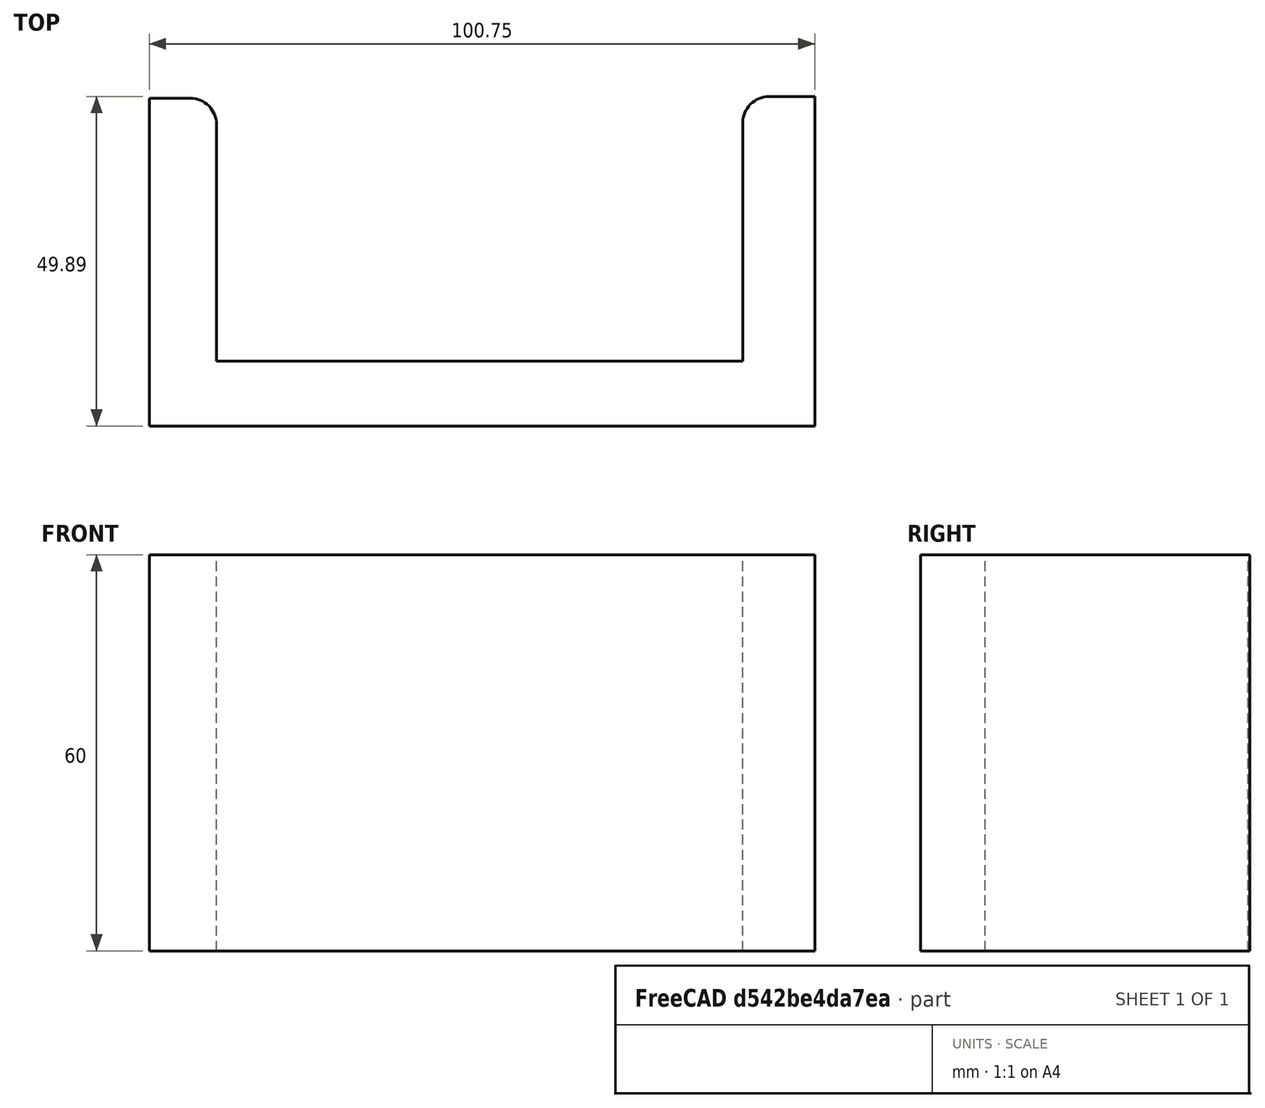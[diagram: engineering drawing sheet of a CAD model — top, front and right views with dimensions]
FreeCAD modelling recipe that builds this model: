
FCSTD DOCUMENT  (FreeCAD 0.21R33668 +26 (Git))
Label: u
License: All rights reserved
LicenseURL: http://en.wikipedia.org/wiki/All_rights_reserved
objects: Part::Extrusion×2, Sketcher::SketchObject×1, Part::Chamfer×1, Part::Fillet×1
note: 5 computed .brp shape members not serialized (recipe doc carries the construction recipe); baked Part::Feature solids carry a one-line shape summary decoded from their .brp

FEATURE [Sketcher::SketchObject] Sketch
  FullyConstrained = false
  sketch-geometry (8):
    g0: LineSegment StartX=-49.9191 StartY=49.6407 StartZ=0 EndX=-49.9191 EndY=0 EndZ=0
    g1: LineSegment StartX=50.8303 StartY=0 StartZ=0 EndX=50.8303 EndY=49.8944 EndZ=0
    g2: LineSegment StartX=39.9179 StartY=49.8944 StartZ=0 EndX=50.8303 EndY=49.8944 EndZ=0
    g3: LineSegment StartX=39.9179 StartY=9.79766 StartZ=0 EndX=39.9179 EndY=49.8944 EndZ=0
    g4: LineSegment StartX=39.9179 StartY=9.79766 StartZ=0 EndX=-39.768 EndY=9.79766 EndZ=0
    g5: LineSegment StartX=-49.9191 StartY=49.6407 StartZ=0 EndX=-39.768 EndY=49.6407 EndZ=0
    g6: LineSegment StartX=-39.768 StartY=49.6407 StartZ=0 EndX=-39.768 EndY=9.79766 EndZ=0
    g7: LineSegment StartX=-49.9191 StartY=0 StartZ=0 EndX=50.8303 EndY=0 EndZ=0
  constraints (17):
    c: PointOnObject(g0,g-1)
    c: Vertical(g0)
    c: PointOnObject(g1,g-1)
    c: Vertical(g1)
    c: Coincident(g2,g1)
    c: Horizontal(g2)
    c: Coincident(g3,g2)
    c: Vertical(g3)
    c: Coincident(g4,g3)
    c: Horizontal(g4)
    c: Coincident(g5,g0)
    c: Horizontal(g5)
    c: Coincident(g6,g5)
    c: Coincident(g6,g4)
    c: Vertical(g6)
    c: Coincident(g7,g0)
    c: Coincident(g7,g1)
FEATURE [Part::Extrusion] Extrude
  Base = -> Sketch
  Dir = (0,0,1)
  DirMode = 2
  FaceMakerClass = Part::FaceMakerBullseye
  LengthFwd = 60
  LengthRev = 0
  Solid = true
  Symmetric = false
FEATURE [Part::Extrusion] Extrude001
  Base = -> Sketch
  Dir = (0,0,1)
  DirMode = 2
  FaceMakerClass = Part::FaceMakerBullseye
  LengthFwd = 60
  LengthRev = 0
  Solid = true
  Symmetric = false
FEATURE [Part::Chamfer] Chamfer
  Base = -> Extrude
  Edges = 2 edges r=2: [Edge2,Edge14]
FEATURE [Part::Fillet] Fillet
  Base = -> Extrude001
  Edges = 2 edges r=4: [Edge2,Edge14]
